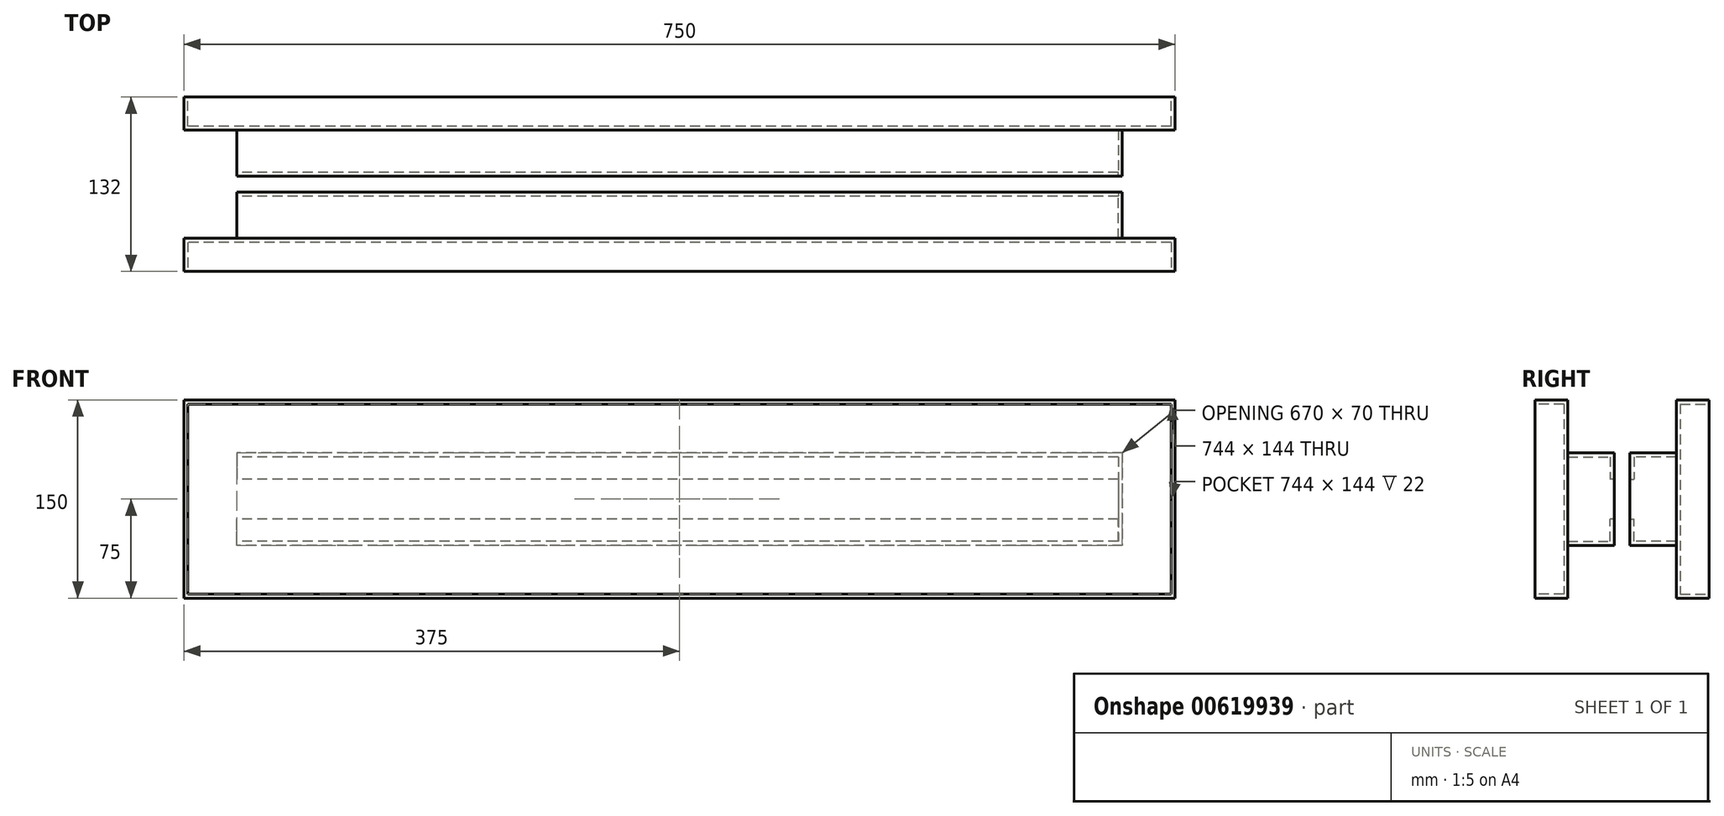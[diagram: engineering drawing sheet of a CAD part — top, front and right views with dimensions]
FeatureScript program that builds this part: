
annotation { "Feature Type Name" : "Feature", "Feature Type Description" : "" }
export const myFeature = defineFeature(function(context is Context, id is Id, definition is map)
    precondition{}
    {
        {
            var Q0;
            Q0=qCreatedBy(makeId("Right.planeOp"),FACE);
            var sketch = newSketch(context, id + "F0", { "sketchPlane" : qUnion([Q0])});
            skLineSegment(sketch, "E0.bottom", {"start": v(41, 75) * mm, "end": v(66, 75) * mm});
            skLineSegment(sketch, "E0.top", {"start": v(41, -75) * mm, "end": v(66, -75) * mm});
            skLineSegment(sketch, "E0.left", {"start": v(41, 75) * mm, "end": v(41, -75) * mm});
            skLineSegment(sketch, "E0.right", {"start": v(66, 75) * mm, "end": v(66, -75) * mm});
            skSolve(sketch);
        }
        {
            var Q0;
            Q0 = qSketchRegion(id + "F0", true);
            extrude(context, id + "F1", {"entities" : qUnion([Q0]), "endBound" : BoundingType.SYMMETRIC, "depth" : 750 * mm, "offsetDistance" : 25 * mm});
        }
        {
            var Q0;
            Q0=makeQuery(id+"F1.opExtrude","SWEPT_FACE",FACE,{"disambiguationData":[OSD([sQuery(id+"F0.wireOp",EDGE,"E0.right")])]});
            var Q1;
            Q1=makeQuery(id+"F1.opExtrude","SWEPT_BODY",BODY,{"disambiguationData":[OSD([sQuery(id+"F0.wireOp",EDGE,"E0.bottom"),sQuery(id+"F0.wireOp",EDGE,"E0.top"),sQuery(id+"F0.wireOp",EDGE,"E0.left"),sQuery(id+"F0.wireOp",EDGE,"E0.right")])]});
            shell(context, id + "F2", {"entities" : qUnion([Q0]), "parts" : qUnion([Q1]), "thickness" : 3 * mm});
        }
        {
            var Q0;
            Q0=qCreatedBy(makeId("Right.planeOp"),FACE);
            var sketch = newSketch(context, id + "F3", { "sketchPlane" : qUnion([Q0])});
            skLineSegment(sketch, "E1", {"start": v(41, 35) * mm, "end": v(6, 35) * mm});
            skLineSegment(sketch, "E2", {"start": v(6, 35) * mm, "end": v(6, 15) * mm});
            skLineSegment(sketch, "E3.0", {"start": v(9, 32) * mm, "end": v(9, 15) * mm});
            skLineSegment(sketch, "E3.1", {"start": v(41, 32) * mm, "end": v(9, 32) * mm});
            skLineSegment(sketch, "E4", {"start": v(41, 35) * mm, "end": v(41, 32) * mm});
            skLineSegment(sketch, "E5", {"start": v(6, 15) * mm, "end": v(9, 15) * mm});
            skLineSegment(sketch, "E6.MirrorCS", {"start": v(41, -35) * mm, "end": v(41, -32) * mm});
            skLineSegment(sketch, "E7.MirrorCS", {"start": v(6, -15) * mm, "end": v(9, -15) * mm});
            skLineSegment(sketch, "E8.MirrorCS", {"start": v(41, -35) * mm, "end": v(6, -35) * mm});
            skLineSegment(sketch, "E9.MirrorCS", {"start": v(6, -35) * mm, "end": v(6, -15) * mm});
            skLineSegment(sketch, "E10.MirrorCS", {"start": v(41, -32) * mm, "end": v(9, -32) * mm});
            skLineSegment(sketch, "E11.MirrorCS", {"start": v(9, -32) * mm, "end": v(9, -15) * mm});
            skSolve(sketch);
        }
        {
            var Q0;
            Q0 = qSketchRegion(id + "F3", true);
            extrude(context, id + "F4", {"entities" : qUnion([Q0]), "operationType" : NewBodyOperationType.ADD, "endBound" : BoundingType.SYMMETRIC, "depth" : 670 * mm, "offsetDistance" : 25 * mm});
        }
        {
            var Q0;
            Q0=makeQuery(id+"F4.opExtrude","CAP_FACE",FACE,{"disambiguationData":[OSD([sQuery(id+"F3.wireOp",EDGE,"E6.MirrorCS"),sQuery(id+"F3.wireOp",EDGE,"E7.MirrorCS"),sQuery(id+"F3.wireOp",EDGE,"E8.MirrorCS"),sQuery(id+"F3.wireOp",EDGE,"E9.MirrorCS"),sQuery(id+"F3.wireOp",EDGE,"E10.MirrorCS"),sQuery(id+"F3.wireOp",EDGE,"E11.MirrorCS")])],"isStart":false});
            var sketch = newSketch(context, id + "F5", { "sketchPlane" : qUnion([Q0])});
            skLineSegment(sketch, "E12.bottom", {"start": v(6, 35) * mm, "end": v(41, 35) * mm});
            skLineSegment(sketch, "E12.top", {"start": v(6, -35) * mm, "end": v(41, -35) * mm});
            skLineSegment(sketch, "E12.left", {"start": v(6, 35) * mm, "end": v(6, -35) * mm});
            skLineSegment(sketch, "E12.right", {"start": v(41, 35) * mm, "end": v(41, -35) * mm});
            skSolve(sketch);
        }
        {
            var Q0;
            Q0 = qSketchRegion(id + "F5", true);
            extrude(context, id + "F6", {"entities" : qUnion([Q0]), "operationType" : NewBodyOperationType.ADD, "oppositeDirection" : true, "depth" : 3 * mm, "offsetDistance" : 25 * mm});
        }
        {
            var Q0;
            Q0=makeQuery(id+"F1.opExtrude","SWEPT_BODY",BODY,{"disambiguationData":[OSD([sQuery(id+"F0.wireOp",EDGE,"E0.bottom"),sQuery(id+"F0.wireOp",EDGE,"E0.top"),sQuery(id+"F0.wireOp",EDGE,"E0.left"),sQuery(id+"F0.wireOp",EDGE,"E0.right")])]});
            var Q1;
            Q1=qCreatedBy(makeId("Front.planeOp"),FACE);
            mirror(context, id + "F7", {"entities" : qUnion([Q0]), "mirrorPlane" : qUnion([Q1])});
        }
    });
